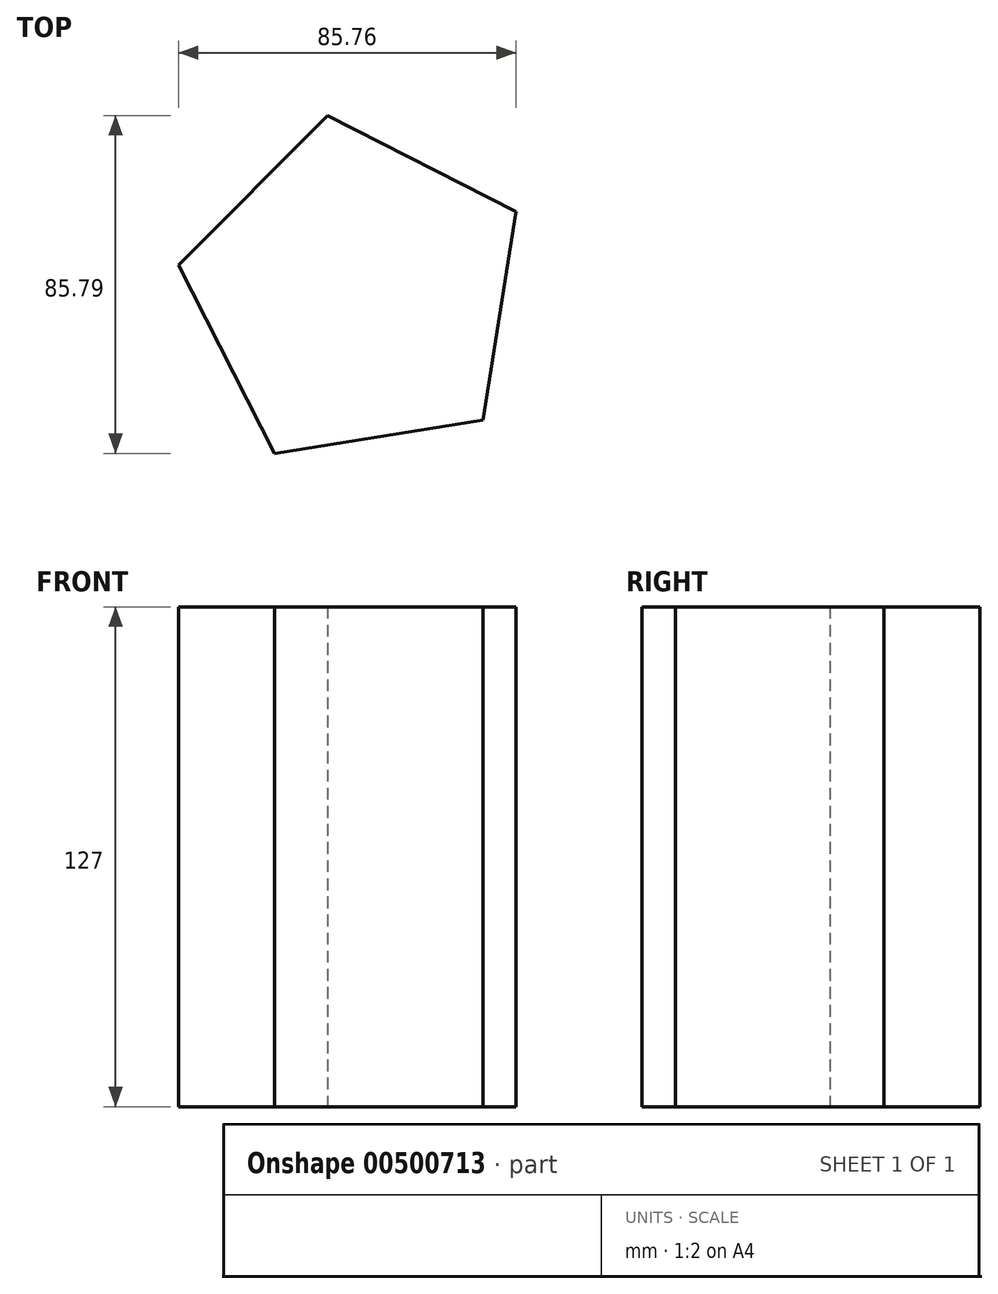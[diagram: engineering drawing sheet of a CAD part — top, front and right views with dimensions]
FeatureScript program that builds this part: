
annotation { "Feature Type Name" : "Feature", "Feature Type Description" : "" }
export const myFeature = defineFeature(function(context is Context, id is Id, definition is map)
    precondition{}
    {
        {
            var Q0;
            Q0=qCreatedBy(makeId("Top.planeOp"),FACE);
            var sketch = newSketch(context, id + "F0", { "sketchPlane" : qUnion([Q0])});
            skCircle(sketch, "E0.cCircle", {"center": v(0, 0) * mm, "radius": 45.65 * mm, "construction": true});
            skLineSegment(sketch, "E0.0", {"start": v(40.66, 20.76) * mm, "end": v(32.31, -32.25) * mm});
            skLineSegment(sketch, "E0.1", {"start": v(32.31, -32.25) * mm, "end": v(-20.69, -40.7) * mm});
            skLineSegment(sketch, "E0.2", {"start": v(-20.69, -40.7) * mm, "end": v(-45.1, 7.1) * mm});
            skLineSegment(sketch, "E0.3", {"start": v(-45.1, 7.1) * mm, "end": v(-7.18, 45.09) * mm});
            skLineSegment(sketch, "E0.4", {"start": v(-7.18, 45.09) * mm, "end": v(40.66, 20.76) * mm});
            skSolve(sketch);
        }
        {
            var Q0;
            Q0=makeQuery(id+"F0.imprint","IMPRINT",FACE,{"disambiguationData":[TD([[makeQuery(id+"F0.imprint","IMPRINT",EDGE,{"derivedFrom":sQuery(id+"F0.wireOp",EDGE,"E0.0")}),-1.0]])]});
            extrude(context, id + "F1", {"entities" : qUnion([Q0]), "depth" : 127 * mm});
        }
    });
